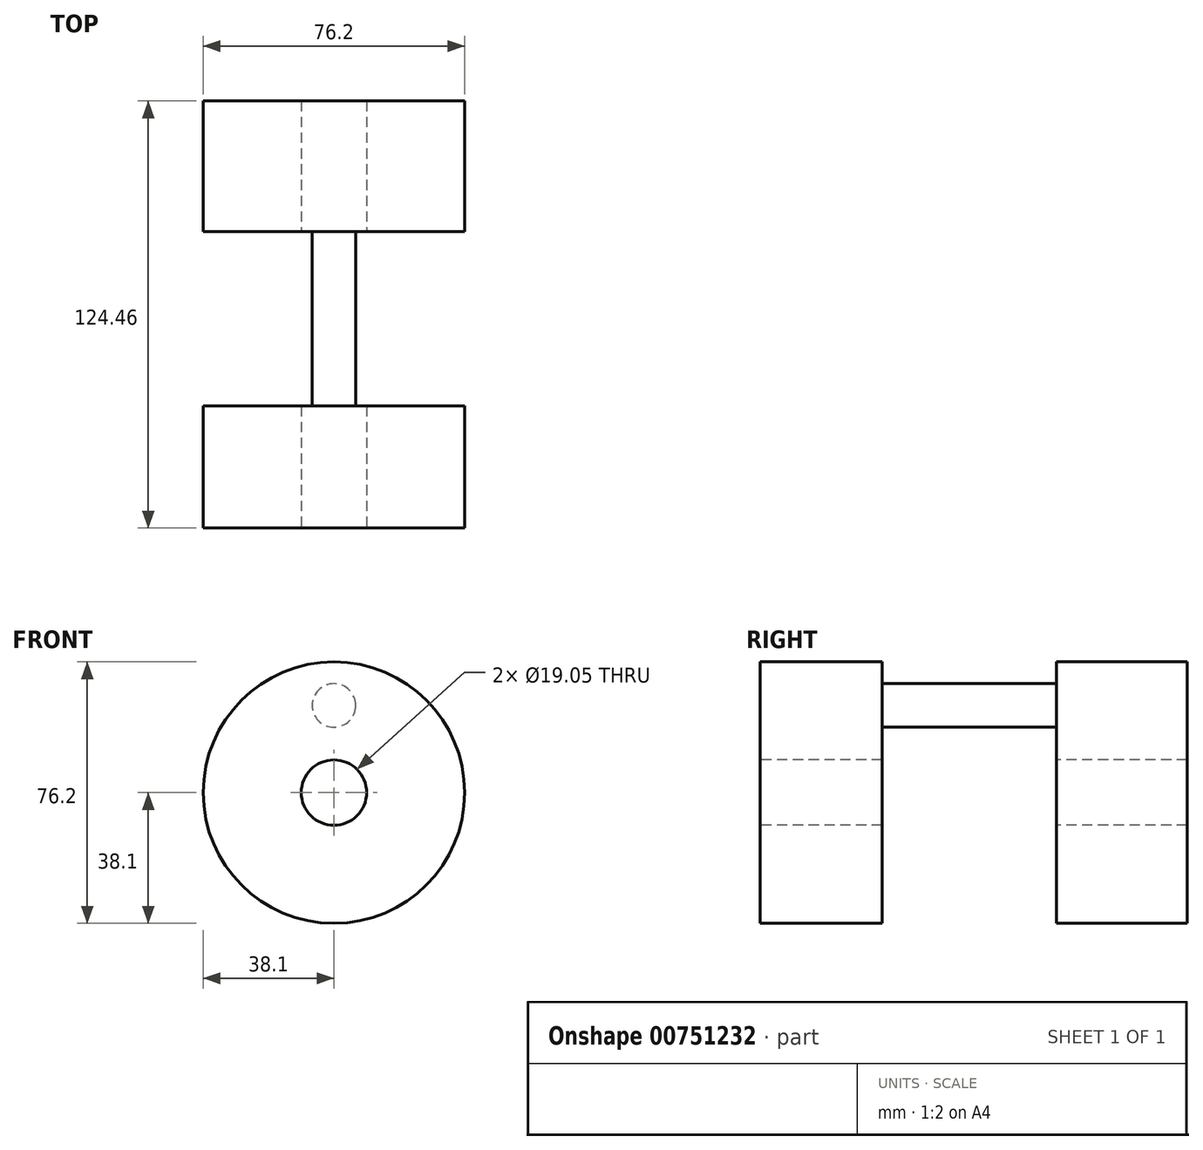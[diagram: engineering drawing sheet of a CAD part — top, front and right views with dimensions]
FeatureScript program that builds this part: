
annotation { "Feature Type Name" : "Feature", "Feature Type Description" : "" }
export const myFeature = defineFeature(function(context is Context, id is Id, definition is map)
    precondition{}
    {
        {
            var Q0;
            Q0=qCreatedBy(makeId("Front.planeOp"),FACE);
            var sketch = newSketch(context, id + "F0", { "sketchPlane" : qUnion([Q0])});
            skCircle(sketch, "E0", {"center": v(0, 0) * mm, "radius": 38.1 * mm});
            skSolve(sketch);
        }
        {
            var Q0;
            Q0 = qSketchRegion(id + "F0", true);
            extrude(context, id + "F1", {"entities" : qUnion([Q0]), "oppositeDirection" : true, "depth" : 63.5 * mm, "offsetDistance" : 25.4 * mm, "hasSecondDirection" : true, "secondDirectionOppositeDirection" : true, "secondDirectionDepth" : 25.4 * mm});
        }
        {
            var Q0;
            Q0=makeQuery(id+"F1.opExtrude","CAP_FACE",FACE,{"disambiguationData":[OSD([sQuery(id+"F0.wireOp",EDGE,"E0")])],"isStart":true});
            var sketch = newSketch(context, id + "F2", { "sketchPlane" : qUnion([Q0])});
            skCircle(sketch, "E1", {"center": v(0, 25.4) * mm, "radius": 6.35 * mm});
            skSolve(sketch);
        }
        {
            var Q0;
            Q0 = qSketchRegion(id + "F2", true);
            extrude(context, id + "F3", {"entities" : qUnion([Q0]), "operationType" : NewBodyOperationType.ADD, "depth" : 50.8 * mm, "offsetDistance" : 25.4 * mm});
        }
        {
            var Q0;
            Q0=makeQuery(id+"F3.opExtrude","CAP_FACE",FACE,{"disambiguationData":[OSD([sQuery(id+"F2.wireOp",EDGE,"E1")])],"isStart":false});
            var sketch = newSketch(context, id + "F4", { "sketchPlane" : qUnion([Q0])});
            skCircle(sketch, "E2", {"center": v(0, 0) * mm, "radius": 38.1 * mm});
            skSolve(sketch);
        }
        {
            var Q0;
            Q0 = qSketchRegion(id + "F4", true);
            extrude(context, id + "F5", {"entities" : qUnion([Q0]), "operationType" : NewBodyOperationType.ADD, "depth" : 35.56 * mm, "offsetDistance" : 25.4 * mm});
        }
        {
            var Q0;
            Q0=makeQuery(id+"F5.opExtrude","CAP_FACE",FACE,{"disambiguationData":[OSD([sQuery(id+"F4.wireOp",EDGE,"E2")])],"isStart":false});
            var sketch = newSketch(context, id + "F6", { "sketchPlane" : qUnion([Q0])});
            skCircle(sketch, "E3", {"center": v(0, 0) * mm, "radius": 9.53 * mm});
            skSolve(sketch);
        }
        {
            var Q0;
            Q0 = qSketchRegion(id + "F6", true);
            extrude(context, id + "F7", {"entities" : qUnion([Q0]), "operationType" : NewBodyOperationType.REMOVE, "endBound" : BoundingType.THROUGH_ALL, "oppositeDirection" : true, "depth" : 25.4 * mm, "offsetDistance" : 25.4 * mm});
        }
    });
